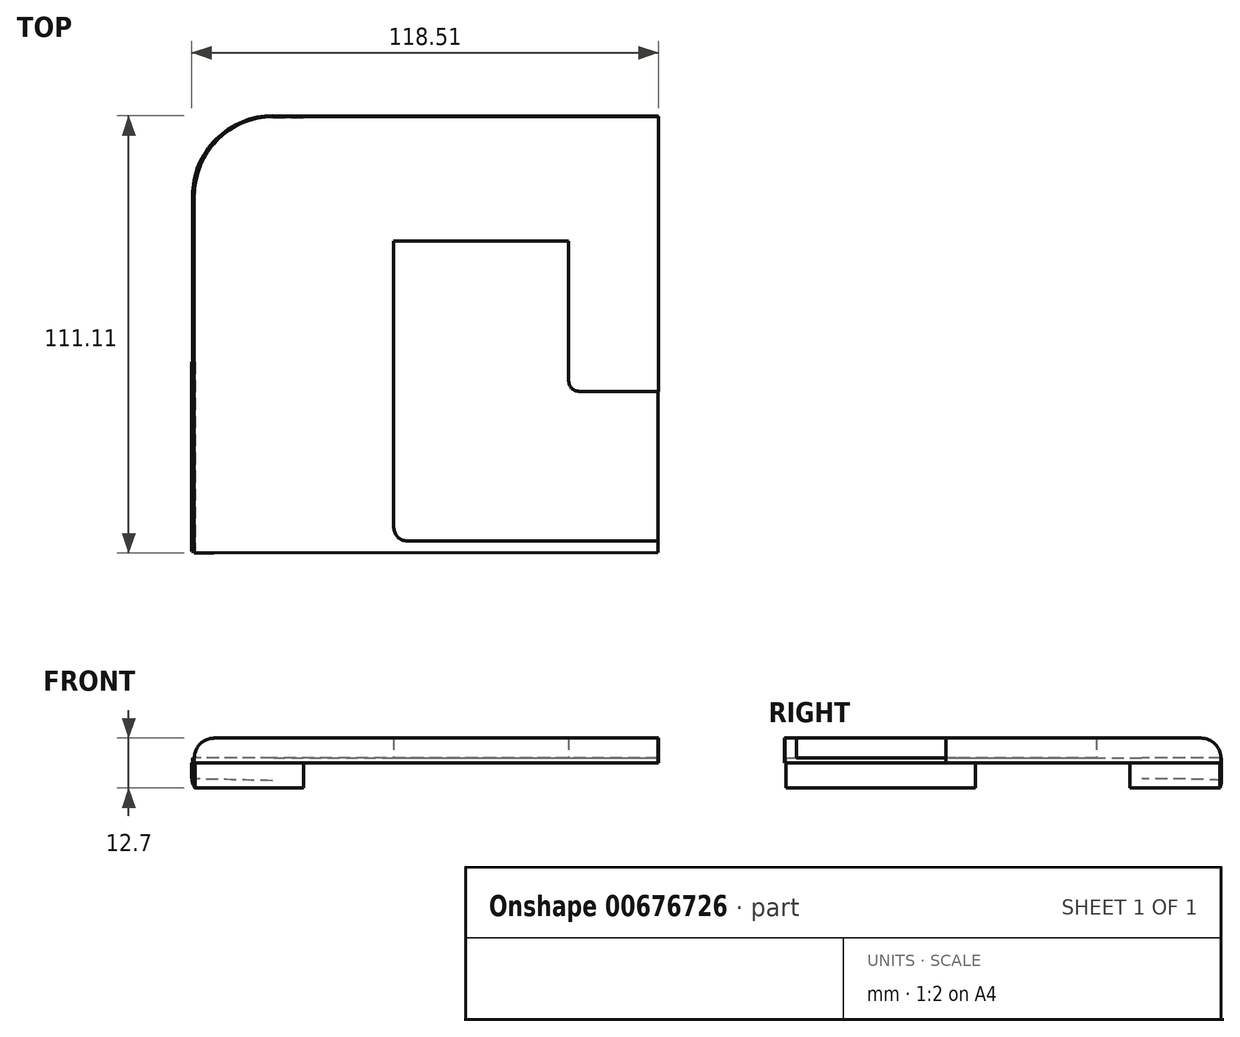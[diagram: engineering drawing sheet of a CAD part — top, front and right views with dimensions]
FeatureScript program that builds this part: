
annotation { "Feature Type Name" : "Feature", "Feature Type Description" : "" }
export const myFeature = defineFeature(function(context is Context, id is Id, definition is map)
    precondition{}
    {
        {
            var Q0;
            Q0=qCreatedBy(makeId("Top.planeOp"),FACE);
            var sketch = newSketch(context, id + "F0", { "sketchPlane" : qUnion([Q0])});
            skLineSegment(sketch, "E0", {"start": v(-57, -48.12) * mm, "end": v(-57, 42.23) * mm});
            skLineSegment(sketch, "E1", {"start": v(-57, -48.12) * mm, "end": v(61.23, -48.12) * mm});
            skLineSegment(sketch, "E2", {"start": v(61.23, -48.12) * mm, "end": v(61.23, 62.53) * mm});
            skLineSegment(sketch, "E3", {"start": v(61.23, 62.53) * mm, "end": v(-36.68, 62.55) * mm});
            skPoint(sketch, "E4.visualSharp", {"position": v(-57, 62.56) * mm});
            skArc(sketch, "E4.filletArc", {"start": v(-36.68, 62.55) * mm, "mid": v(-51.05, 56.6) * mm, "end": v(-57, 42.23) * mm});
            skSolve(sketch);
        }
        {
            var Q0;
            Q0=qSketchRegion(id+"F0",true);
            extrude(context, id + "F1", {"entities" : qUnion([Q0]), "depth" : 1.27 * mm, "offsetDistance" : 25.4 * mm});
        }
        {
            var Q0;
            Q0=qCreatedBy(makeId("Top.planeOp"),FACE);
            var sketch = newSketch(context, id + "F2", { "sketchPlane" : qUnion([Q0])});
            skLineSegment(sketch, "E5", {"start": v(-28.79, 62.5) * mm, "end": v(-36.74, 62.5) * mm});
            skLineSegment(sketch, "E6", {"start": v(-56.99, 42.26) * mm, "end": v(-56.99, 39.26) * mm});
            skPoint(sketch, "E7.visualSharp", {"position": v(-56.99, 62.5) * mm});
            skArc(sketch, "E7.filletArc", {"start": v(-36.74, 62.5) * mm, "mid": v(-51.06, 56.57) * mm, "end": v(-56.99, 42.26) * mm});
            skLineSegment(sketch, "E8", {"start": v(-56.99, 39.26) * mm, "end": v(-56.99, 42.26) * mm});
            skLineSegment(sketch, "E9", {"start": v(-56.99, 39.26) * mm, "end": v(-56.41, 39.26) * mm});
            skLineSegment(sketch, "E10", {"start": v(-56.41, 39.26) * mm, "end": v(-56.41, 42.26) * mm});
            skLineSegment(sketch, "E11", {"start": v(-36.53, 62.14) * mm, "end": v(-28.8, 62.14) * mm});
            skLineSegment(sketch, "E12", {"start": v(-28.8, 62.14) * mm, "end": v(-28.79, 62.5) * mm});
            skPoint(sketch, "E13.visualSharp", {"position": v(-56.41, 62.14) * mm});
            skArc(sketch, "E13.filletArc", {"start": v(-36.53, 62.14) * mm, "mid": v(-50.59, 56.32) * mm, "end": v(-56.41, 42.26) * mm});
            skLineSegment(sketch, "E14", {"start": v(-57.2, 0) * mm, "end": v(-57.2, -48.1) * mm});
            skLineSegment(sketch, "E15", {"start": v(-57.2, 0) * mm, "end": v(-56.4, 0) * mm});
            skLineSegment(sketch, "E16", {"start": v(-56.4, 0) * mm, "end": v(-56.4, -48.1) * mm});
            skLineSegment(sketch, "E17", {"start": v(-56.4, -48.1) * mm, "end": v(-57.2, -48.1) * mm});
            skSolve(sketch);
        }
        {
            var Q0;
            Q0=qSketchRegion(id+"F2",true);
            extrude(context, id + "F3", {"entities" : qUnion([Q0]), "operationType" : NewBodyOperationType.ADD, "depth" : -6.35 * mm, "offsetDistance" : 25.4 * mm});
        }
        {
            var Q0;
            Q0=qCreatedBy(makeId("Top.planeOp"),FACE);
            var sketch = newSketch(context, id + "F4", { "sketchPlane" : qUnion([Q0])});
            skLineSegment(sketch, "E18", {"start": v(61.23, -48.34) * mm, "end": v(61.23, -45.45) * mm});
            skLineSegment(sketch, "E19", {"start": v(61.23, -45.45) * mm, "end": v(-2.48, -45.45) * mm});
            skLineSegment(sketch, "E20", {"start": v(-5.89, -42.04) * mm, "end": v(-5.89, 30.78) * mm});
            skLineSegment(sketch, "E21", {"start": v(-5.89, 30.78) * mm, "end": v(38.56, 30.78) * mm});
            skLineSegment(sketch, "E22", {"start": v(38.56, 30.78) * mm, "end": v(38.56, -4.84) * mm});
            skLineSegment(sketch, "E23", {"start": v(41.17, -7.45) * mm, "end": v(61.31, -7.45) * mm});
            skLineSegment(sketch, "E24", {"start": v(61.31, -7.45) * mm, "end": v(61.31, 62.38) * mm});
            skLineSegment(sketch, "E25", {"start": v(61.31, 62.38) * mm, "end": v(-36.48, 62.38) * mm});
            skLineSegment(sketch, "E26", {"start": v(-56.57, 42.29) * mm, "end": v(-56.57, -48.56) * mm});
            skLineSegment(sketch, "E27", {"start": v(-56.57, -48.56) * mm, "end": v(61.23, -48.34) * mm});
            skPoint(sketch, "E28.visualSharp", {"position": v(-56.57, 62.38) * mm});
            skArc(sketch, "E28.filletArc", {"start": v(-36.48, 62.38) * mm, "mid": v(-50.69, 56.5) * mm, "end": v(-56.57, 42.29) * mm});
            skPoint(sketch, "E29.visualSharp", {"position": v(-5.89, -45.45) * mm});
            skArc(sketch, "E29.filletArc", {"start": v(-5.89, -42.04) * mm, "mid": v(-4.9, -44.45) * mm, "end": v(-2.48, -45.45) * mm});
            skPoint(sketch, "E30.visualSharp", {"position": v(38.56, -7.45) * mm});
            skArc(sketch, "E30.filletArc", {"start": v(38.56, -4.84) * mm, "mid": v(39.32, -6.68) * mm, "end": v(41.17, -7.45) * mm});
            skSolve(sketch);
        }
        {
            var Q0;
            Q0=makeQuery(id+"F4.imprint","IMPRINT",FACE,{"disambiguationData":[TD([[makeQuery(id+"F4.imprint","IMPRINT",EDGE,{"derivedFrom":sQuery(id+"F4.wireOp",EDGE,"E18")}),1.0]])]});
            var Q1;
            Q1=qSketchRegion(id+"F4",true);
            extrude(context, id + "F5", {"entities" : qUnion([Q0, Q1]), "operationType" : NewBodyOperationType.ADD, "depth" : 6.35 * mm, "offsetDistance" : 25.4 * mm});
        }
        {
            var Q0;
            Q0=makeQuery(id+"F5.opExtrude","CAP_EDGE",EDGE,{"disambiguationData":[OSD([sQuery(id+"F4.wireOp",EDGE,"E25")])],"isStart":false});
            fillet(context, id + "F6", {"entities" : qUnion([Q0]), "radius" : 5.08 * mm, "tangentPropagation" : true, "allowEdgeOverflow" : false});
        }
        {
            var Q0;
            Q0=makeQuery(id+"F3.opExtrude","CAP_EDGE",EDGE,{"disambiguationData":[OSD([sQuery(id+"F2.wireOp",EDGE,"E5")])],"isStart":false});
            fillet(context, id + "F7", {"entities" : qUnion([Q0]), "radius" : 5.08 * mm, "tangentPropagation" : true, "allowEdgeOverflow" : false});
        }
        {
            var Q0;
            Q0=makeQuery(id+"F3.opExtrude","CAP_EDGE",EDGE,{"disambiguationData":[OSD([sQuery(id+"F2.wireOp",EDGE,"E14")])],"isStart":false});
            fillet(context, id + "F8", {"entities" : qUnion([Q0]), "radius" : 5.08 * mm, "tangentPropagation" : true, "allowEdgeOverflow" : false});
        }
    });
